# Revit family: PROOX Double toilet roll holder EN
name_source: partatom
category: Furniture
revit_build: Autodesk Revit 2014 (Build: 20130308_1515(x64)
units: mm (PartAtom-declared; Revit-internal decimal feet)

## types (2) — shared parameters
BIM objects producer = www.BIMtelligent.eu
Manufacturer = PROOX Ltd.
Product data sheet = http://www.proox.com
URL = http://www.proox.com

## per-type parameters (varying)
| type | Cost | Description | EAN-No. | Material | Model | Specification |
| ONE pure | 215 $ | double toilet roll holder PROOX ONE pure made from stainless steel | 9120050350090 | PROOX Stainless steel, brushed | PU-300 | Double toilet roll holder made out of stainless steel. Surface with fine brushed structure. Cover 1.5 mm thickness. Intended for wall mounting. Perforated filling indicator with 4mm drillings. For two rolls with max. 140mm width and 130mm diameter. Second roll drops into position when flap is moved upwards. Works without spindle system. Lock not visible. Includes stainless steel screws and anchors. |
| ONE dark passion | 245 $ | double toilet roll holder PROOX ONE dark passion made from aluminum black anodized | 9120050350212 | PROOX Aluminum, black anodised | DP-300 | Double toilet roll holder made out from glass pearl blasted and black anodised aluminum. Cover 3 mm thickness. Intended for wall mounting. Perforated filling indicator with 4mm drillings. For two rolls with max. 140mm width and 130mm diameter. Second roll drops into position when flap is moved upwards. Works without spindle system. Lock not visible. Includes stainless steel screws and anchors. |

note: column(s) folded — value = type name in every type: Type Comments

## geometry (parser evidence)
native form markers: Sweep x1
no freeform markers — native parametric forms only
